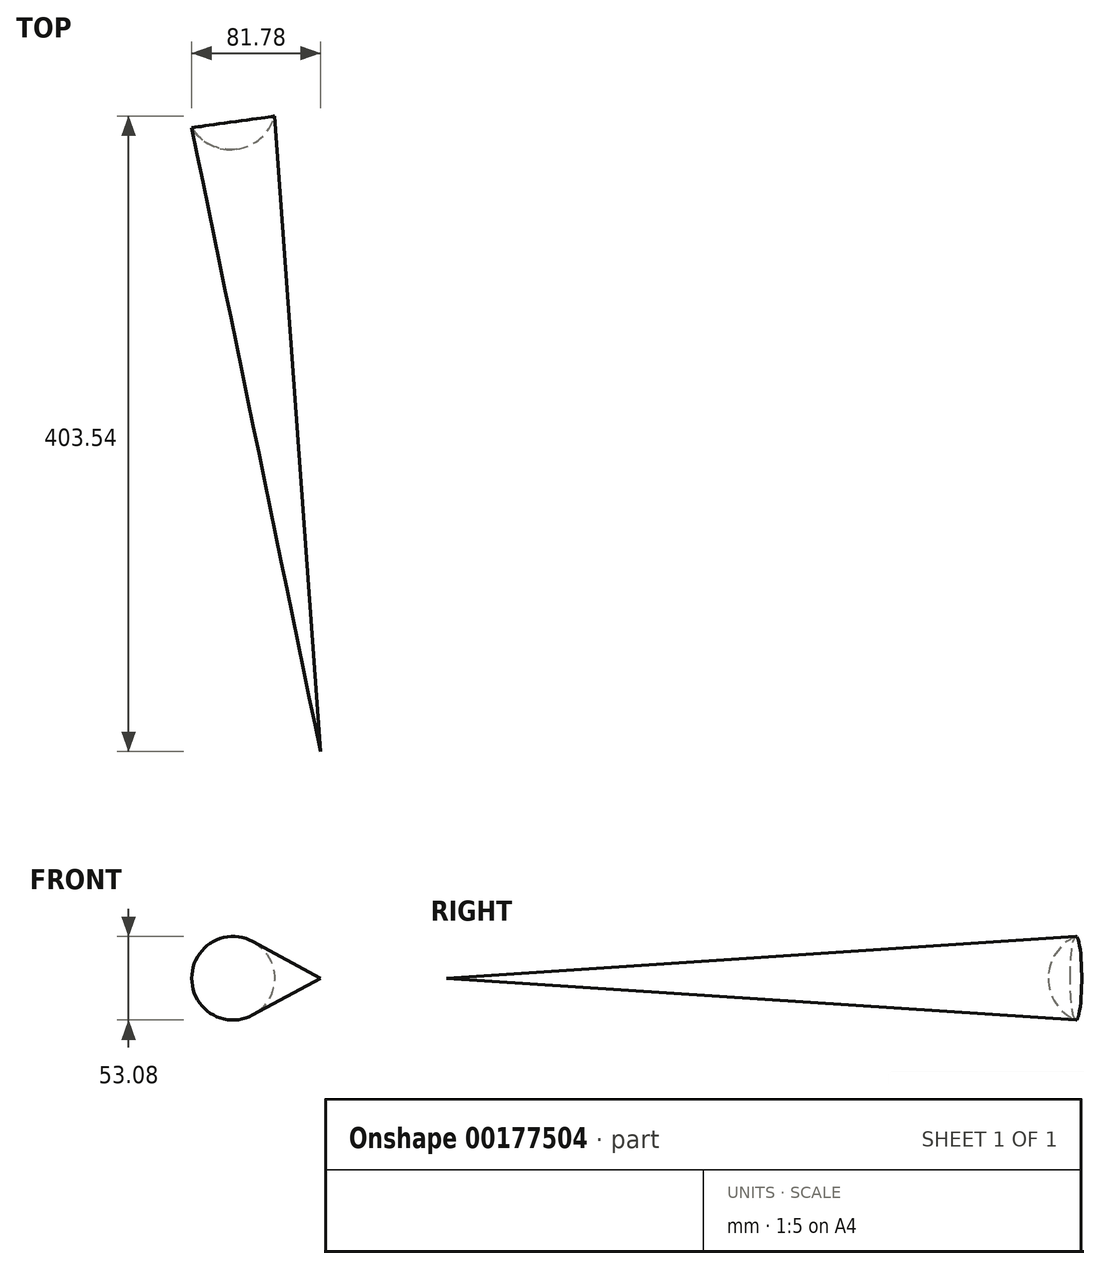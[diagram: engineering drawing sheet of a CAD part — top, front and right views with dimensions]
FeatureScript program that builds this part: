
annotation { "Feature Type Name" : "Feature", "Feature Type Description" : "" }
export const myFeature = defineFeature(function(context is Context, id is Id, definition is map)
    precondition{}
    {
        {
            var Q0;
            Q0=qCreatedBy(makeId("Top.planeOp"),FACE);
            var sketch = newSketch(context, id + "F0", { "sketchPlane" : qUnion([Q0])});
            skCircle(sketch, "E0", {"center": v(0, 0) * mm, "radius": 28.89 * mm});
            skSolve(sketch);
        }
        {
            var Q0;
            Q0=makeQuery(id+"F0.imprint","IMPRINT",FACE,{"disambiguationData":[TD([[makeQuery(id+"F0.imprint","IMPRINT",EDGE,{"derivedFrom":sQuery(id+"F0.wireOp",EDGE,"E0")}),1.0]])]});
            var sketch = newSketch(context, id + "F1", { "sketchPlane" : qUnion([Q0])});
            skLineSegment(sketch, "E1", {"start": v(0, 0) * mm, "end": v(57.07, -411.2) * mm});
            skLineSegment(sketch, "E2", {"start": v(57.07, -411.2) * mm, "end": v(-27.8, 0) * mm});
            skLineSegment(sketch, "E3", {"start": v(0, 0) * mm, "end": v(-27.8, 0) * mm});
            skSolve(sketch);
        }
        {
            var Q0;
            {var subQ0=sQuery(id+"F1.wireOp",EDGE,"E2");var subQ1=sQuery(id+"F1.wireOp",EDGE,"E1");var subQ2=makeQuery(id+"F1.imprint","INTERSECT",VERTEX,{"derivedFrom":[subQ1,subQ0]});Q0=makeQuery(id+"F1.imprint","IMPRINT",FACE,{"disambiguationData":[TD([[makeQuery(id+"F1.imprint","IMPRINT",EDGE,{"disambiguationData":[TD([[subQ2,1.0]])],"derivedFrom":subQ1}),-1.0]])]});}
            var Q1;
            Q1=sQuery(id+"F1.wireOp",EDGE,"E1");
            revolve(context, id + "F2", {"entities" : qUnion([Q0]), "axis" : qUnion([Q1]), "revolveType" : RevolveType.FULL});
        }
    });
